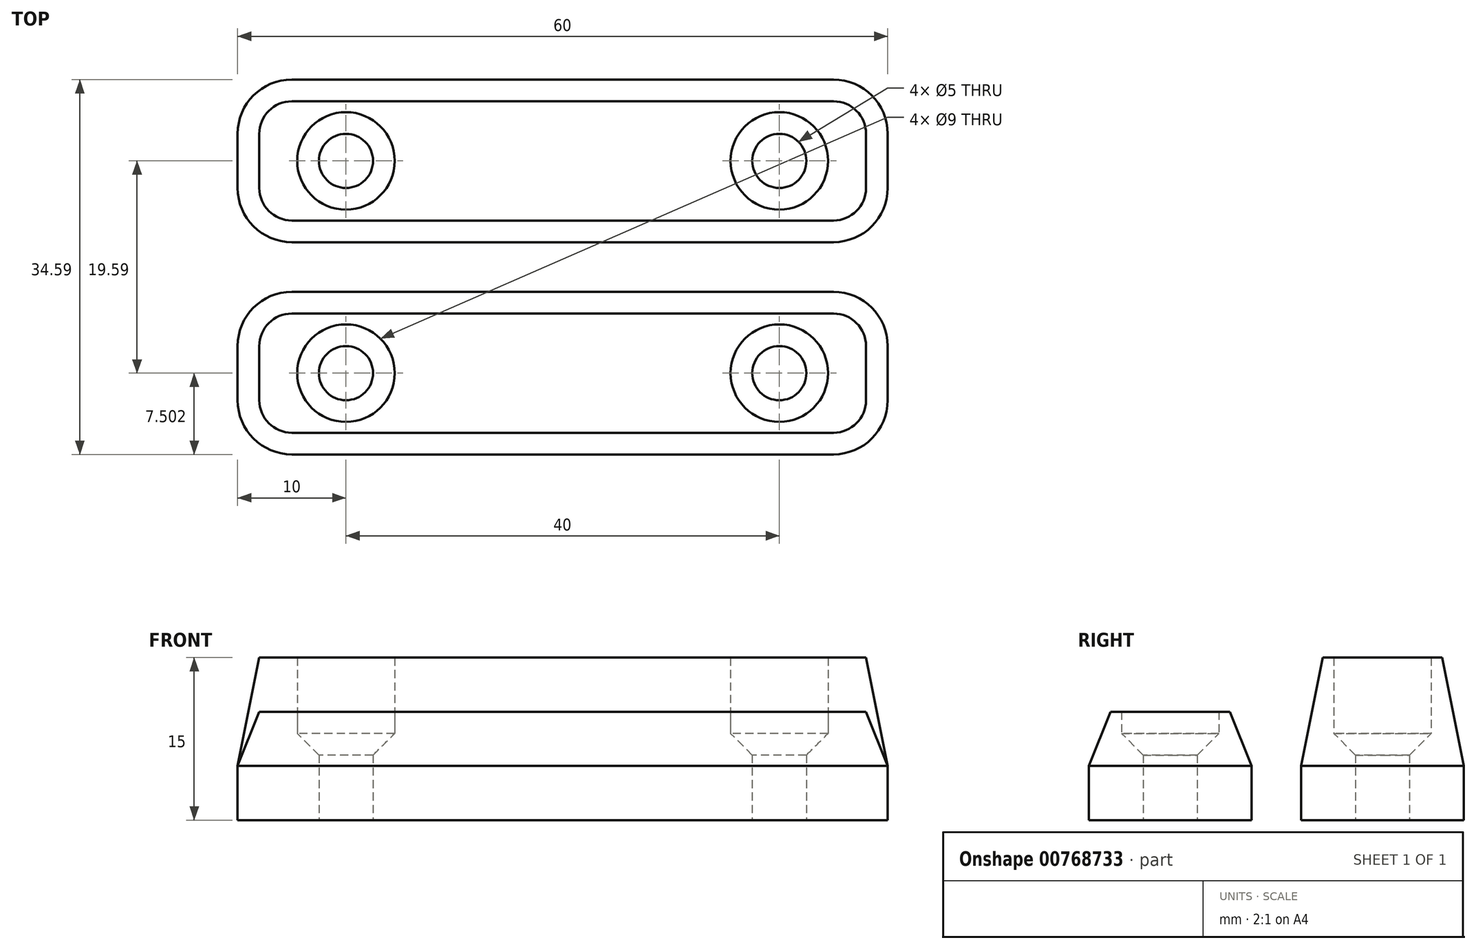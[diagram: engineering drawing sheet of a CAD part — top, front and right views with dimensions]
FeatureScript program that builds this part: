
annotation { "Feature Type Name" : "Feature", "Feature Type Description" : "" }
export const myFeature = defineFeature(function(context is Context, id is Id, definition is map)
    precondition{}
    {
        {
            var Q0;
            Q0=qCreatedBy(makeId("Top.planeOp"),FACE);
            var sketch = newSketch(context, id + "F0", { "sketchPlane" : qUnion([Q0])});
            skLineSegment(sketch, "E0.bottom", {"start": v(5, -26.72) * mm, "end": v(55, -26.72) * mm});
            skLineSegment(sketch, "E0.top", {"start": v(5, -41.72) * mm, "end": v(55, -41.72) * mm});
            skLineSegment(sketch, "E0.left", {"start": v(0, -31.72) * mm, "end": v(0, -36.72) * mm});
            skLineSegment(sketch, "E0.right", {"start": v(60, -31.72) * mm, "end": v(60, -36.72) * mm});
            skPoint(sketch, "E1.visualSharp", {"position": v(0, -26.72) * mm});
            skArc(sketch, "E1.filletArc", {"start": v(5, -26.72) * mm, "mid": v(1.46, -28.18) * mm, "end": v(0, -31.72) * mm});
            skPoint(sketch, "E2.visualSharp", {"position": v(0, -41.72) * mm});
            skArc(sketch, "E2.filletArc", {"start": v(0, -36.72) * mm, "mid": v(1.46, -40.25) * mm, "end": v(5, -41.72) * mm});
            skPoint(sketch, "E3.visualSharp", {"position": v(60, -41.72) * mm});
            skArc(sketch, "E3.filletArc", {"start": v(55, -41.72) * mm, "mid": v(58.54, -40.25) * mm, "end": v(60, -36.72) * mm});
            skPoint(sketch, "E4.visualSharp", {"position": v(60, -26.72) * mm});
            skArc(sketch, "E4.filletArc", {"start": v(60, -31.72) * mm, "mid": v(58.54, -28.18) * mm, "end": v(55, -26.72) * mm});
            skLineSegment(sketch, "E5", {"start": v(0, -34.22) * mm, "end": v(60, -34.22) * mm, "construction": true});
            skLineSegment(sketch, "E6", {"start": v(30, -26.72) * mm, "end": v(30, -41.72) * mm, "construction": true});
            skLineSegment(sketch, "E7", {"start": v(10, -26.72) * mm, "end": v(10, -41.72) * mm, "construction": true});
            skLineSegment(sketch, "E8", {"start": v(50, -26.72) * mm, "end": v(50, -41.72) * mm, "construction": true});
            skCircle(sketch, "E9", {"center": v(10, -34.22) * mm, "radius": 2.5 * mm});
            skCircle(sketch, "E10", {"center": v(50, -34.22) * mm, "radius": 2.5 * mm});
            skCircle(sketch, "E11", {"center": v(10, -34.22) * mm, "radius": 4.5 * mm});
            skCircle(sketch, "E12", {"center": v(50, -34.22) * mm, "radius": 4.5 * mm});
            skLineSegment(sketch, "E13.bottom", {"start": v(5, -7.13) * mm, "end": v(55, -7.13) * mm});
            skLineSegment(sketch, "E13.top", {"start": v(5, -22.13) * mm, "end": v(55, -22.13) * mm});
            skLineSegment(sketch, "E13.left", {"start": v(0, -12.13) * mm, "end": v(0, -17.13) * mm});
            skLineSegment(sketch, "E13.right", {"start": v(60, -12.13) * mm, "end": v(60, -17.13) * mm});
            skPoint(sketch, "E14.visualSharp", {"position": v(0, -7.13) * mm});
            skArc(sketch, "E14.filletArc", {"start": v(5, -7.13) * mm, "mid": v(1.46, -8.6) * mm, "end": v(0, -12.13) * mm});
            skPoint(sketch, "E15.visualSharp", {"position": v(0, -22.13) * mm});
            skArc(sketch, "E15.filletArc", {"start": v(0, -17.13) * mm, "mid": v(1.46, -20.66) * mm, "end": v(5, -22.13) * mm});
            skPoint(sketch, "E16.visualSharp", {"position": v(60, -22.13) * mm});
            skArc(sketch, "E16.filletArc", {"start": v(55, -22.13) * mm, "mid": v(58.54, -20.66) * mm, "end": v(60, -17.13) * mm});
            skPoint(sketch, "E17.visualSharp", {"position": v(60, -7.13) * mm});
            skArc(sketch, "E17.filletArc", {"start": v(60, -12.13) * mm, "mid": v(58.54, -8.6) * mm, "end": v(55, -7.13) * mm});
            skLineSegment(sketch, "E18", {"start": v(0, -14.63) * mm, "end": v(60, -14.63) * mm, "construction": true});
            skLineSegment(sketch, "E19", {"start": v(30, -7.13) * mm, "end": v(30, -22.13) * mm, "construction": true});
            skLineSegment(sketch, "E20", {"start": v(10, -7.13) * mm, "end": v(10, -22.13) * mm, "construction": true});
            skLineSegment(sketch, "E21", {"start": v(50, -7.13) * mm, "end": v(50, -22.13) * mm, "construction": true});
            skCircle(sketch, "E22", {"center": v(10, -14.63) * mm, "radius": 2.5 * mm});
            skCircle(sketch, "E23", {"center": v(50, -14.63) * mm, "radius": 2.5 * mm});
            skCircle(sketch, "E24", {"center": v(10, -14.63) * mm, "radius": 4.5 * mm});
            skCircle(sketch, "E25", {"center": v(50, -14.63) * mm, "radius": 4.5 * mm});
            skSolve(sketch);
        }
        {
            var Q0;
            Q0=makeQuery(id+"F0.imprint","IMPRINT",FACE,{"disambiguationData":[TD([[makeQuery(id+"F0.imprint","IMPRINT",EDGE,{"derivedFrom":sQuery(id+"F0.wireOp",EDGE,"E0.bottom")}),-1.0]])]});
            extrude(context, id + "F1", {"entities" : qUnion([Q0]), "depth" : 10 * mm, "offsetDistance" : 25 * mm});
        }
        {
            var Q0;
            Q0=makeQuery(id+"F0.imprint","IMPRINT",FACE,{"disambiguationData":[TD([[makeQuery(id+"F0.imprint","IMPRINT",EDGE,{"derivedFrom":sQuery(id+"F0.wireOp",EDGE,"Pow4mqjb-eiVI-kAR0-DN75-39RLUVyTiGvO")}),-1.0]])]});
            var Q1;
            Q1=makeQuery(id+"F0.imprint","IMPRINT",FACE,{"disambiguationData":[TD([[makeQuery(id+"F0.imprint","IMPRINT",EDGE,{"derivedFrom":sQuery(id+"F0.wireOp",EDGE,"rFEiqGDG-daG7-hRB3-QPuE-xKi68pjn7Zn6")}),-1.0]])]});
            var Q2;
            Q2=makeQuery(id+"F0.imprint","IMPRINT",FACE,{"disambiguationData":[TD([[makeQuery(id+"F0.imprint","IMPRINT",EDGE,{"derivedFrom":sQuery(id+"F0.wireOp",EDGE,"E10")}),-1.0]])]});
            var Q3;
            Q3=makeQuery(id+"F0.imprint","IMPRINT",FACE,{"disambiguationData":[TD([[makeQuery(id+"F0.imprint","IMPRINT",EDGE,{"derivedFrom":sQuery(id+"F0.wireOp",EDGE,"E9")}),-1.0]])]});
            var Q4;
            Q4=makeQuery(id+"F0.imprint","IMPRINT",FACE,{"disambiguationData":[TD([[makeQuery(id+"F0.imprint","IMPRINT",EDGE,{"derivedFrom":sQuery(id+"F0.wireOp",EDGE,"E22")}),-1.0]])]});
            var Q5;
            Q5=makeQuery(id+"F0.imprint","IMPRINT",FACE,{"disambiguationData":[TD([[makeQuery(id+"F0.imprint","IMPRINT",EDGE,{"derivedFrom":sQuery(id+"F0.wireOp",EDGE,"E23")}),-1.0]])]});
            extrude(context, id + "F2", {"entities" : qUnion([Q0, Q1, Q2, Q3, Q4, Q5]), "operationType" : NewBodyOperationType.ADD, "depth" : 8 * mm, "offsetDistance" : 25 * mm});
        }
        {
            var Q0;
            Q0=makeQuery(id+"F1.opExtrude","CAP_EDGE",EDGE,{"disambiguationData":[OSD([sQuery(id+"F0.wireOp",EDGE,"E0.bottom")])],"isStart":false});
            chamfer(context, id + "F3", {"entities" : qUnion([Q0]), "chamferType" : ChamferType.TWO_OFFSETS, "width1" : 5 * mm, "oppositeDirection" : false, "width2" : 2 * mm, "tangentPropagation" : true});
        }
        {
            var Q0;
            Q0=makeQuery(id+"F2.opExtrude","CAP_EDGE",EDGE,{"disambiguationData":[OSD([sQuery(id+"F0.wireOp",EDGE,"Pow4mqjb-eiVI-kAR0-DN75-39RLUVyTiGvO")])],"isStart":false});
            var Q1;
            Q1=makeQuery(id+"F2.opExtrude","CAP_EDGE",EDGE,{"disambiguationData":[OSD([sQuery(id+"F0.wireOp",EDGE,"rFEiqGDG-daG7-hRB3-QPuE-xKi68pjn7Zn6")])],"isStart":false});
            var Q2;
            Q2=makeQuery(id+"F2.opExtrude","CAP_EDGE",EDGE,{"disambiguationData":[OSD([sQuery(id+"F0.wireOp",EDGE,"E10")])],"isStart":false});
            var Q3;
            Q3=makeQuery(id+"F2.opExtrude","CAP_EDGE",EDGE,{"disambiguationData":[OSD([sQuery(id+"F0.wireOp",EDGE,"E9")])],"isStart":false});
            var Q4;
            Q4=makeQuery(id+"F2.opExtrude","CAP_EDGE",EDGE,{"disambiguationData":[OSD([sQuery(id+"F0.wireOp",EDGE,"E22")])],"isStart":false});
            var Q5;
            Q5=makeQuery(id+"F2.opExtrude","CAP_EDGE",EDGE,{"disambiguationData":[OSD([sQuery(id+"F0.wireOp",EDGE,"E23")])],"isStart":false});
            chamfer(context, id + "F4", {"entities" : qUnion([Q0, Q1, Q2, Q3, Q4, Q5]), "width" : 2 * mm, "tangentPropagation" : true});
        }
        {
            var Q0;
            Q0=makeQuery(id+"F0.imprint","IMPRINT",FACE,{"disambiguationData":[TD([[makeQuery(id+"F0.imprint","IMPRINT",EDGE,{"derivedFrom":sQuery(id+"F0.wireOp",EDGE,"E13.bottom")}),-1.0]])]});
            extrude(context, id + "F5", {"entities" : qUnion([Q0]), "operationType" : NewBodyOperationType.ADD, "depth" : 15 * mm, "offsetDistance" : 25 * mm});
        }
        {
            var Q0;
            Q0=makeQuery(id+"F5.opExtrude","CAP_EDGE",EDGE,{"disambiguationData":[OSD([sQuery(id+"F0.wireOp",EDGE,"E13.bottom")])],"isStart":false});
            chamfer(context, id + "F6", {"entities" : qUnion([Q0]), "chamferType" : ChamferType.TWO_OFFSETS, "width1" : 10 * mm, "oppositeDirection" : false, "width2" : 2 * mm, "tangentPropagation" : true});
        }
    });
